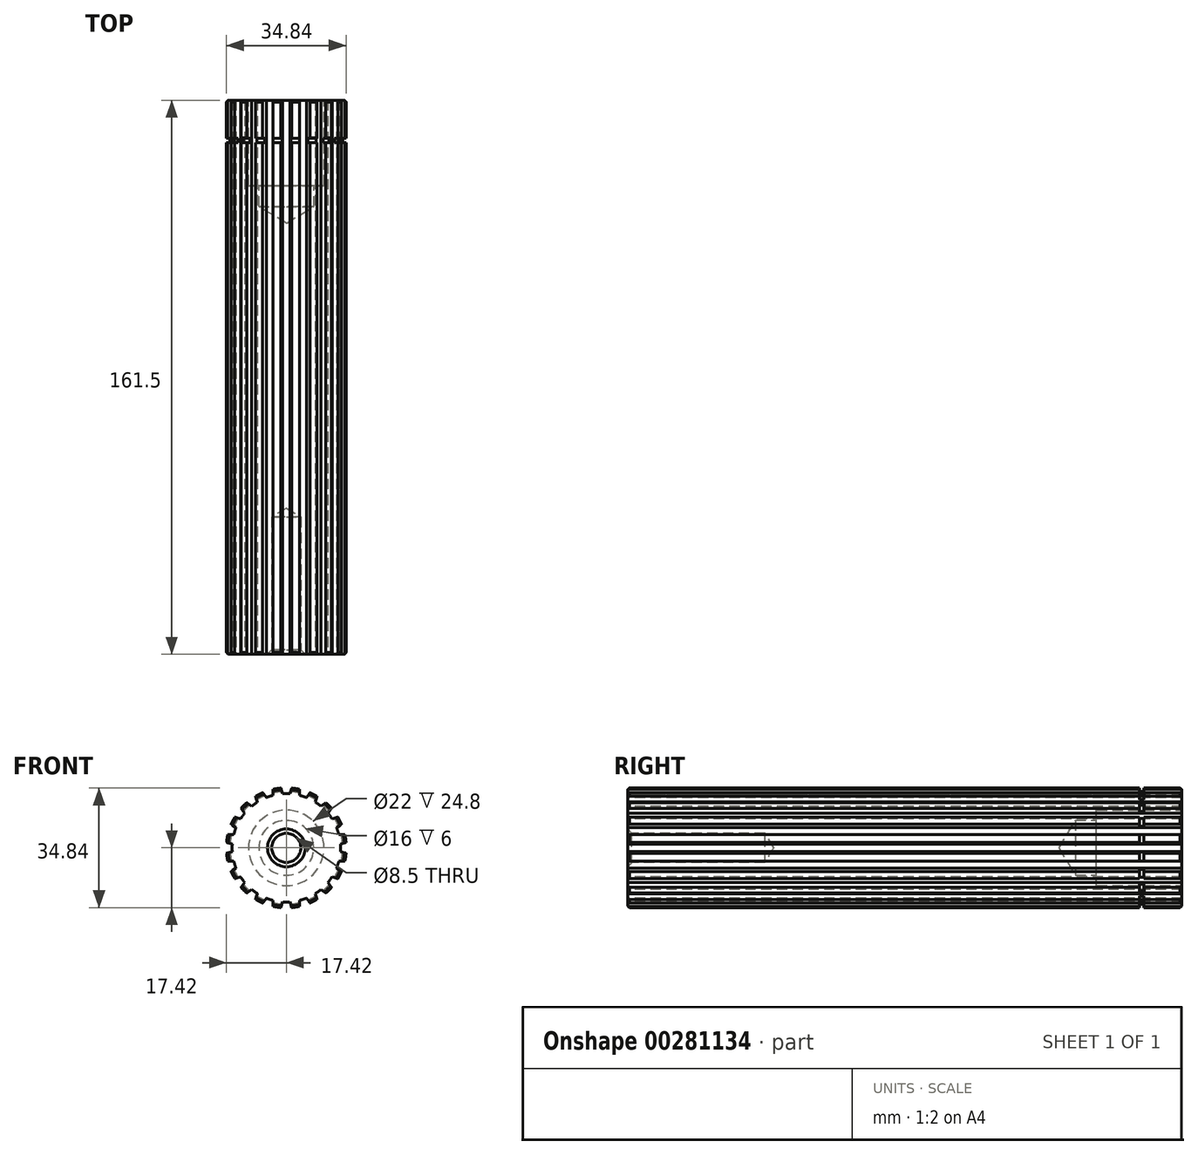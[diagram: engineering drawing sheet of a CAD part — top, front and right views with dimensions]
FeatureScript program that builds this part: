
annotation { "Feature Type Name" : "Feature", "Feature Type Description" : "" }
export const myFeature = defineFeature(function(context is Context, id is Id, definition is map)
    precondition{}
    {
        {
            var Q0;
            Q0=qCreatedBy(makeId("Front.planeOp"),FACE);
            var sketch = newSketch(context, id + "F0", { "sketchPlane" : qUnion([Q0])});
            skArc(sketch, "E0", {"start": v(-5.85, -14.65) * mm, "mid": v(-4.88, -15) * mm, "end": v(-3.88, -15.3) * mm});
            skLineSegment(sketch, "E1", {"start": v(-3.88, -15.3) * mm, "end": v(-3.88, -17.06) * mm});
            skLineSegment(sketch, "E2", {"start": v(-6.89, -16.08) * mm, "end": v(-5.85, -14.65) * mm});
            skArc(sketch, "E3", {"start": v(-3.88, -17.06) * mm, "mid": v(-2.74, -17.28) * mm, "end": v(-1.58, -17.42) * mm});
            skLineSegment(sketch, "E4", {"start": v(-1.58, -17.42) * mm, "end": v(-1.04, -15.75) * mm});
            skArc(sketch, "E5", {"start": v(-1.04, -15.75) * mm, "mid": v(0, -15.78) * mm, "end": v(1.04, -15.75) * mm});
            skLineSegment(sketch, "E6", {"start": v(1.04, -15.75) * mm, "end": v(1.58, -17.42) * mm});
            skArc(sketch, "E7", {"start": v(1.58, -17.42) * mm, "mid": v(2.74, -17.28) * mm, "end": v(3.88, -17.06) * mm});
            skLineSegment(sketch, "E8", {"start": v(3.88, -17.06) * mm, "end": v(3.88, -15.3) * mm});
            skArc(sketch, "E9", {"start": v(3.88, -15.3) * mm, "mid": v(4.88, -15) * mm, "end": v(5.85, -14.65) * mm});
            skLineSegment(sketch, "E10", {"start": v(5.85, -14.65) * mm, "end": v(6.89, -16.08) * mm});
            skArc(sketch, "E11", {"start": v(6.89, -16.08) * mm, "mid": v(7.94, -15.59) * mm, "end": v(8.96, -15.02) * mm});
            skLineSegment(sketch, "E12", {"start": v(8.96, -15.02) * mm, "end": v(8.42, -13.35) * mm});
            skArc(sketch, "E13", {"start": v(8.42, -13.35) * mm, "mid": v(9.28, -12.77) * mm, "end": v(10.1, -12.13) * mm});
            skLineSegment(sketch, "E14", {"start": v(10.1, -12.13) * mm, "end": v(11.52, -13.17) * mm});
            skArc(sketch, "E15", {"start": v(11.52, -13.17) * mm, "mid": v(12.37, -12.37) * mm, "end": v(13.17, -11.52) * mm});
            skLineSegment(sketch, "E16", {"start": v(13.17, -11.52) * mm, "end": v(12.13, -10.1) * mm});
            skArc(sketch, "E17", {"start": v(12.13, -10.1) * mm, "mid": v(12.77, -9.28) * mm, "end": v(13.35, -8.42) * mm});
            skLineSegment(sketch, "E18", {"start": v(13.35, -8.42) * mm, "end": v(15.02, -8.96) * mm});
            skArc(sketch, "E19", {"start": v(15.02, -8.96) * mm, "mid": v(15.59, -7.94) * mm, "end": v(16.08, -6.89) * mm});
            skLineSegment(sketch, "E20", {"start": v(16.08, -6.89) * mm, "end": v(14.65, -5.85) * mm});
            skArc(sketch, "E21", {"start": v(14.65, -5.85) * mm, "mid": v(15, -4.88) * mm, "end": v(15.3, -3.88) * mm});
            skLineSegment(sketch, "E22", {"start": v(15.3, -3.88) * mm, "end": v(17.06, -3.88) * mm});
            skArc(sketch, "E23", {"start": v(17.06, -3.88) * mm, "mid": v(17.28, -2.74) * mm, "end": v(17.42, -1.58) * mm});
            skLineSegment(sketch, "E24", {"start": v(17.42, -1.58) * mm, "end": v(15.75, -1.04) * mm});
            skArc(sketch, "E25", {"start": v(15.75, -1.04) * mm, "mid": v(15.78, 0) * mm, "end": v(15.75, 1.04) * mm});
            skLineSegment(sketch, "E26", {"start": v(15.75, 1.04) * mm, "end": v(17.42, 1.58) * mm});
            skArc(sketch, "E27", {"start": v(17.42, 1.58) * mm, "mid": v(17.28, 2.74) * mm, "end": v(17.06, 3.88) * mm});
            skLineSegment(sketch, "E28", {"start": v(17.06, 3.88) * mm, "end": v(15.3, 3.88) * mm});
            skArc(sketch, "E29", {"start": v(15.3, 3.88) * mm, "mid": v(15, 4.88) * mm, "end": v(14.65, 5.85) * mm});
            skLineSegment(sketch, "E30", {"start": v(14.65, 5.85) * mm, "end": v(16.08, 6.89) * mm});
            skArc(sketch, "E31", {"start": v(16.08, 6.89) * mm, "mid": v(15.59, 7.94) * mm, "end": v(15.02, 8.96) * mm});
            skLineSegment(sketch, "E32", {"start": v(15.02, 8.96) * mm, "end": v(13.35, 8.42) * mm});
            skArc(sketch, "E33", {"start": v(13.35, 8.42) * mm, "mid": v(12.77, 9.28) * mm, "end": v(12.13, 10.1) * mm});
            skLineSegment(sketch, "E34", {"start": v(12.13, 10.1) * mm, "end": v(13.17, 11.52) * mm});
            skArc(sketch, "E35", {"start": v(13.17, 11.52) * mm, "mid": v(12.37, 12.37) * mm, "end": v(11.52, 13.17) * mm});
            skLineSegment(sketch, "E36", {"start": v(11.52, 13.17) * mm, "end": v(10.1, 12.13) * mm});
            skArc(sketch, "E37", {"start": v(10.1, 12.13) * mm, "mid": v(9.28, 12.77) * mm, "end": v(8.42, 13.35) * mm});
            skLineSegment(sketch, "E38", {"start": v(8.42, 13.35) * mm, "end": v(8.96, 15.02) * mm});
            skArc(sketch, "E39", {"start": v(8.96, 15.02) * mm, "mid": v(7.94, 15.59) * mm, "end": v(6.89, 16.08) * mm});
            skLineSegment(sketch, "E40", {"start": v(6.89, 16.08) * mm, "end": v(5.85, 14.65) * mm});
            skArc(sketch, "E41", {"start": v(5.85, 14.65) * mm, "mid": v(4.88, 15) * mm, "end": v(3.88, 15.3) * mm});
            skLineSegment(sketch, "E42", {"start": v(3.88, 15.3) * mm, "end": v(3.88, 17.06) * mm});
            skArc(sketch, "E43", {"start": v(3.88, 17.06) * mm, "mid": v(2.74, 17.28) * mm, "end": v(1.58, 17.42) * mm});
            skLineSegment(sketch, "E44", {"start": v(1.58, 17.42) * mm, "end": v(1.04, 15.75) * mm});
            skArc(sketch, "E45", {"start": v(1.04, 15.75) * mm, "mid": v(0, 15.78) * mm, "end": v(-1.04, 15.75) * mm});
            skLineSegment(sketch, "E46", {"start": v(-1.04, 15.75) * mm, "end": v(-1.58, 17.42) * mm});
            skArc(sketch, "E47", {"start": v(-1.58, 17.42) * mm, "mid": v(-2.74, 17.28) * mm, "end": v(-3.88, 17.06) * mm});
            skLineSegment(sketch, "E48", {"start": v(-3.88, 17.06) * mm, "end": v(-3.88, 15.3) * mm});
            skArc(sketch, "E49", {"start": v(-3.88, 15.3) * mm, "mid": v(-4.88, 15) * mm, "end": v(-5.85, 14.65) * mm});
            skLineSegment(sketch, "E50", {"start": v(-5.85, 14.65) * mm, "end": v(-6.89, 16.08) * mm});
            skArc(sketch, "E51", {"start": v(-6.89, 16.08) * mm, "mid": v(-7.94, 15.59) * mm, "end": v(-8.96, 15.02) * mm});
            skLineSegment(sketch, "E52", {"start": v(-8.96, 15.02) * mm, "end": v(-8.42, 13.35) * mm});
            skArc(sketch, "E53", {"start": v(-8.42, 13.35) * mm, "mid": v(-9.28, 12.77) * mm, "end": v(-10.1, 12.13) * mm});
            skLineSegment(sketch, "E54", {"start": v(-10.1, 12.13) * mm, "end": v(-11.52, 13.17) * mm});
            skArc(sketch, "E55", {"start": v(-11.52, 13.17) * mm, "mid": v(-12.37, 12.37) * mm, "end": v(-13.17, 11.52) * mm});
            skLineSegment(sketch, "E56", {"start": v(-13.17, 11.52) * mm, "end": v(-12.13, 10.1) * mm});
            skArc(sketch, "E57", {"start": v(-12.13, 10.1) * mm, "mid": v(-12.77, 9.28) * mm, "end": v(-13.35, 8.42) * mm});
            skLineSegment(sketch, "E58", {"start": v(-13.35, 8.42) * mm, "end": v(-15.02, 8.96) * mm});
            skArc(sketch, "E59", {"start": v(-15.02, 8.96) * mm, "mid": v(-15.59, 7.94) * mm, "end": v(-16.08, 6.89) * mm});
            skLineSegment(sketch, "E60", {"start": v(-16.08, 6.89) * mm, "end": v(-14.65, 5.85) * mm});
            skArc(sketch, "E61", {"start": v(-14.65, 5.85) * mm, "mid": v(-15, 4.88) * mm, "end": v(-15.3, 3.88) * mm});
            skLineSegment(sketch, "E62", {"start": v(-15.3, 3.88) * mm, "end": v(-17.06, 3.88) * mm});
            skArc(sketch, "E63", {"start": v(-17.06, 3.88) * mm, "mid": v(-17.28, 2.74) * mm, "end": v(-17.42, 1.58) * mm});
            skLineSegment(sketch, "E64", {"start": v(-17.42, 1.58) * mm, "end": v(-15.75, 1.04) * mm});
            skArc(sketch, "E65", {"start": v(-15.75, 1.04) * mm, "mid": v(-15.78, 0) * mm, "end": v(-15.75, -1.04) * mm});
            skLineSegment(sketch, "E66", {"start": v(-15.75, -1.04) * mm, "end": v(-17.42, -1.58) * mm});
            skArc(sketch, "E67", {"start": v(-17.42, -1.58) * mm, "mid": v(-17.28, -2.74) * mm, "end": v(-17.06, -3.88) * mm});
            skLineSegment(sketch, "E68", {"start": v(-17.06, -3.88) * mm, "end": v(-15.3, -3.88) * mm});
            skArc(sketch, "E69", {"start": v(-15.3, -3.88) * mm, "mid": v(-15, -4.88) * mm, "end": v(-14.65, -5.85) * mm});
            skLineSegment(sketch, "E70", {"start": v(-14.65, -5.85) * mm, "end": v(-16.08, -6.89) * mm});
            skArc(sketch, "E71", {"start": v(-16.08, -6.89) * mm, "mid": v(-15.59, -7.94) * mm, "end": v(-15.02, -8.96) * mm});
            skLineSegment(sketch, "E72", {"start": v(-15.02, -8.96) * mm, "end": v(-13.35, -8.42) * mm});
            skArc(sketch, "E73", {"start": v(-13.35, -8.42) * mm, "mid": v(-12.77, -9.28) * mm, "end": v(-12.13, -10.1) * mm});
            skLineSegment(sketch, "E74", {"start": v(-12.13, -10.1) * mm, "end": v(-13.17, -11.52) * mm});
            skArc(sketch, "E75", {"start": v(-13.17, -11.52) * mm, "mid": v(-12.37, -12.37) * mm, "end": v(-11.52, -13.17) * mm});
            skLineSegment(sketch, "E76", {"start": v(-11.52, -13.17) * mm, "end": v(-10.1, -12.13) * mm});
            skArc(sketch, "E77", {"start": v(-10.1, -12.13) * mm, "mid": v(-9.28, -12.77) * mm, "end": v(-8.42, -13.35) * mm});
            skLineSegment(sketch, "E78", {"start": v(-8.42, -13.35) * mm, "end": v(-8.96, -15.02) * mm});
            skArc(sketch, "E79", {"start": v(-8.96, -15.02) * mm, "mid": v(-7.94, -15.59) * mm, "end": v(-6.89, -16.08) * mm});
            skLineSegment(sketch, "E80", {"start": v(0, -20.5) * mm, "end": v(0, 20.5) * mm, "construction": true});
            skLineSegment(sketch, "E81", {"start": v(-20.5, 0) * mm, "end": v(20.5, 0) * mm, "construction": true});
            skSolve(sketch);
        }
        {
            var Q0;
            Q0 = qSketchRegion(id + "F0", true);
            extrude(context, id + "F1", {"entities" : qUnion([Q0]), "oppositeDirection" : true, "depth" : 161.5 * mm});
        }
        {
            var Q0;
            Q0=makeQuery(id+"F1.opExtrude","CAP_FACE",FACE,{"disambiguationData":[OSD([sQuery(id+"F0.wireOp",EDGE,"E0"),sQuery(id+"F0.wireOp",EDGE,"E1"),sQuery(id+"F0.wireOp",EDGE,"E2"),sQuery(id+"F0.wireOp",EDGE,"E3"),sQuery(id+"F0.wireOp",EDGE,"E4"),sQuery(id+"F0.wireOp",EDGE,"E5"),sQuery(id+"F0.wireOp",EDGE,"E6"),sQuery(id+"F0.wireOp",EDGE,"E7"),sQuery(id+"F0.wireOp",EDGE,"E8"),sQuery(id+"F0.wireOp",EDGE,"E9"),sQuery(id+"F0.wireOp",EDGE,"E10"),sQuery(id+"F0.wireOp",EDGE,"E11"),sQuery(id+"F0.wireOp",EDGE,"E12"),sQuery(id+"F0.wireOp",EDGE,"E13"),sQuery(id+"F0.wireOp",EDGE,"E14"),sQuery(id+"F0.wireOp",EDGE,"E15"),sQuery(id+"F0.wireOp",EDGE,"E16"),sQuery(id+"F0.wireOp",EDGE,"E17"),sQuery(id+"F0.wireOp",EDGE,"E18"),sQuery(id+"F0.wireOp",EDGE,"E19"),sQuery(id+"F0.wireOp",EDGE,"E20"),sQuery(id+"F0.wireOp",EDGE,"E21"),sQuery(id+"F0.wireOp",EDGE,"E22"),sQuery(id+"F0.wireOp",EDGE,"E23"),sQuery(id+"F0.wireOp",EDGE,"E24"),sQuery(id+"F0.wireOp",EDGE,"E25"),sQuery(id+"F0.wireOp",EDGE,"E26"),sQuery(id+"F0.wireOp",EDGE,"E27"),sQuery(id+"F0.wireOp",EDGE,"E28"),sQuery(id+"F0.wireOp",EDGE,"E29"),sQuery(id+"F0.wireOp",EDGE,"E30"),sQuery(id+"F0.wireOp",EDGE,"E31"),sQuery(id+"F0.wireOp",EDGE,"E32"),sQuery(id+"F0.wireOp",EDGE,"E33"),sQuery(id+"F0.wireOp",EDGE,"E34"),sQuery(id+"F0.wireOp",EDGE,"E35"),sQuery(id+"F0.wireOp",EDGE,"E36"),sQuery(id+"F0.wireOp",EDGE,"E37"),sQuery(id+"F0.wireOp",EDGE,"E38"),sQuery(id+"F0.wireOp",EDGE,"E39"),sQuery(id+"F0.wireOp",EDGE,"E40"),sQuery(id+"F0.wireOp",EDGE,"E41"),sQuery(id+"F0.wireOp",EDGE,"E42"),sQuery(id+"F0.wireOp",EDGE,"E43"),sQuery(id+"F0.wireOp",EDGE,"E44"),sQuery(id+"F0.wireOp",EDGE,"E45"),sQuery(id+"F0.wireOp",EDGE,"E46"),sQuery(id+"F0.wireOp",EDGE,"E47"),sQuery(id+"F0.wireOp",EDGE,"E48"),sQuery(id+"F0.wireOp",EDGE,"E49"),sQuery(id+"F0.wireOp",EDGE,"E50"),sQuery(id+"F0.wireOp",EDGE,"E51"),sQuery(id+"F0.wireOp",EDGE,"E52"),sQuery(id+"F0.wireOp",EDGE,"E53"),sQuery(id+"F0.wireOp",EDGE,"E54"),sQuery(id+"F0.wireOp",EDGE,"E55"),sQuery(id+"F0.wireOp",EDGE,"E56"),sQuery(id+"F0.wireOp",EDGE,"E57"),sQuery(id+"F0.wireOp",EDGE,"E58"),sQuery(id+"F0.wireOp",EDGE,"E59"),sQuery(id+"F0.wireOp",EDGE,"E60"),sQuery(id+"F0.wireOp",EDGE,"E61"),sQuery(id+"F0.wireOp",EDGE,"E62"),sQuery(id+"F0.wireOp",EDGE,"E63"),sQuery(id+"F0.wireOp",EDGE,"E64"),sQuery(id+"F0.wireOp",EDGE,"E65"),sQuery(id+"F0.wireOp",EDGE,"E66"),sQuery(id+"F0.wireOp",EDGE,"E67"),sQuery(id+"F0.wireOp",EDGE,"E68"),sQuery(id+"F0.wireOp",EDGE,"E69"),sQuery(id+"F0.wireOp",EDGE,"E70"),sQuery(id+"F0.wireOp",EDGE,"E71"),sQuery(id+"F0.wireOp",EDGE,"E72"),sQuery(id+"F0.wireOp",EDGE,"E73"),sQuery(id+"F0.wireOp",EDGE,"E74"),sQuery(id+"F0.wireOp",EDGE,"E75"),sQuery(id+"F0.wireOp",EDGE,"E76"),sQuery(id+"F0.wireOp",EDGE,"E77"),sQuery(id+"F0.wireOp",EDGE,"E78"),sQuery(id+"F0.wireOp",EDGE,"E79")])],"isStart":false});
            var sketch = newSketch(context, id + "F2", { "sketchPlane" : qUnion([Q0])});
            skPoint(sketch, "E82", {"position": v(0, 0) * mm});
            skCircle(sketch, "E83", {"center": v(0, 0) * mm, "radius": 11 * mm});
            skSolve(sketch);
        }
        {
            var Q0;
            Q0=sQuery(id+"F2.wireOp",VERTEX,"E82");
            var Q1;
            Q1=makeQuery(id+"F1.opExtrude","SWEPT_BODY",BODY,{"disambiguationData":[OSD([sQuery(id+"F0.wireOp",EDGE,"E0"),sQuery(id+"F0.wireOp",EDGE,"E1"),sQuery(id+"F0.wireOp",EDGE,"E2"),sQuery(id+"F0.wireOp",EDGE,"E3"),sQuery(id+"F0.wireOp",EDGE,"E4"),sQuery(id+"F0.wireOp",EDGE,"E5"),sQuery(id+"F0.wireOp",EDGE,"E6"),sQuery(id+"F0.wireOp",EDGE,"E7"),sQuery(id+"F0.wireOp",EDGE,"E8"),sQuery(id+"F0.wireOp",EDGE,"E9"),sQuery(id+"F0.wireOp",EDGE,"E10"),sQuery(id+"F0.wireOp",EDGE,"E11"),sQuery(id+"F0.wireOp",EDGE,"E12"),sQuery(id+"F0.wireOp",EDGE,"E13"),sQuery(id+"F0.wireOp",EDGE,"E14"),sQuery(id+"F0.wireOp",EDGE,"E15"),sQuery(id+"F0.wireOp",EDGE,"E16"),sQuery(id+"F0.wireOp",EDGE,"E17"),sQuery(id+"F0.wireOp",EDGE,"E18"),sQuery(id+"F0.wireOp",EDGE,"E19"),sQuery(id+"F0.wireOp",EDGE,"E20"),sQuery(id+"F0.wireOp",EDGE,"E21"),sQuery(id+"F0.wireOp",EDGE,"E22"),sQuery(id+"F0.wireOp",EDGE,"E23"),sQuery(id+"F0.wireOp",EDGE,"E24"),sQuery(id+"F0.wireOp",EDGE,"E25"),sQuery(id+"F0.wireOp",EDGE,"E26"),sQuery(id+"F0.wireOp",EDGE,"E27"),sQuery(id+"F0.wireOp",EDGE,"E28"),sQuery(id+"F0.wireOp",EDGE,"E29"),sQuery(id+"F0.wireOp",EDGE,"E30"),sQuery(id+"F0.wireOp",EDGE,"E31"),sQuery(id+"F0.wireOp",EDGE,"E32"),sQuery(id+"F0.wireOp",EDGE,"E33"),sQuery(id+"F0.wireOp",EDGE,"E34"),sQuery(id+"F0.wireOp",EDGE,"E35"),sQuery(id+"F0.wireOp",EDGE,"E36"),sQuery(id+"F0.wireOp",EDGE,"E37"),sQuery(id+"F0.wireOp",EDGE,"E38"),sQuery(id+"F0.wireOp",EDGE,"E39"),sQuery(id+"F0.wireOp",EDGE,"E40"),sQuery(id+"F0.wireOp",EDGE,"E41"),sQuery(id+"F0.wireOp",EDGE,"E42"),sQuery(id+"F0.wireOp",EDGE,"E43"),sQuery(id+"F0.wireOp",EDGE,"E44"),sQuery(id+"F0.wireOp",EDGE,"E45"),sQuery(id+"F0.wireOp",EDGE,"E46"),sQuery(id+"F0.wireOp",EDGE,"E47"),sQuery(id+"F0.wireOp",EDGE,"E48"),sQuery(id+"F0.wireOp",EDGE,"E49"),sQuery(id+"F0.wireOp",EDGE,"E50"),sQuery(id+"F0.wireOp",EDGE,"E51"),sQuery(id+"F0.wireOp",EDGE,"E52"),sQuery(id+"F0.wireOp",EDGE,"E53"),sQuery(id+"F0.wireOp",EDGE,"E54"),sQuery(id+"F0.wireOp",EDGE,"E55"),sQuery(id+"F0.wireOp",EDGE,"E56"),sQuery(id+"F0.wireOp",EDGE,"E57"),sQuery(id+"F0.wireOp",EDGE,"E58"),sQuery(id+"F0.wireOp",EDGE,"E59"),sQuery(id+"F0.wireOp",EDGE,"E60"),sQuery(id+"F0.wireOp",EDGE,"E61"),sQuery(id+"F0.wireOp",EDGE,"E62"),sQuery(id+"F0.wireOp",EDGE,"E63"),sQuery(id+"F0.wireOp",EDGE,"E64"),sQuery(id+"F0.wireOp",EDGE,"E65"),sQuery(id+"F0.wireOp",EDGE,"E66"),sQuery(id+"F0.wireOp",EDGE,"E67"),sQuery(id+"F0.wireOp",EDGE,"E68"),sQuery(id+"F0.wireOp",EDGE,"E69"),sQuery(id+"F0.wireOp",EDGE,"E70"),sQuery(id+"F0.wireOp",EDGE,"E71"),sQuery(id+"F0.wireOp",EDGE,"E72"),sQuery(id+"F0.wireOp",EDGE,"E73"),sQuery(id+"F0.wireOp",EDGE,"E74"),sQuery(id+"F0.wireOp",EDGE,"E75"),sQuery(id+"F0.wireOp",EDGE,"E76"),sQuery(id+"F0.wireOp",EDGE,"E77"),sQuery(id+"F0.wireOp",EDGE,"E78"),sQuery(id+"F0.wireOp",EDGE,"E79")])]});
            hole(context, id + "F3", {"style" : HoleStyle.C_SINK, "endStyle" : HoleEndStyle.BLIND, "holeDiameter" : 16 * mm, "cSinkDiameter" : 17 * mm, "cSinkAngle" : 90 * degree, "holeDepth" : 31 * mm, "tappedDepth" : 12 * mm, "tapClearance" : 3, "locations" : qUnion([Q0]), "scope" : qUnion([Q1])});
        }
        {
            var Q0;
            Q0=makeQuery(id+"F2.imprint","IMPRINT",FACE,{"disambiguationData":[TD([[makeQuery(id+"F2.imprint","IMPRINT",EDGE,{"derivedFrom":sQuery(id+"F2.wireOp",EDGE,"E83")}),1.0]])]});
            extrude(context, id + "F4", {"entities" : qUnion([Q0]), "operationType" : NewBodyOperationType.REMOVE, "oppositeDirection" : true, "depth" : 25 * mm});
        }
        {
            var Q0;
            Q0=makeQuery(id+"F2.imprint","IMPRINT",FACE,{"disambiguationData":[TD([[makeQuery(id+"F2.imprint","IMPRINT",EDGE,{"derivedFrom":sQuery(id+"F2.wireOp",EDGE,"E83")}),-1.0]])]});
            cPlane(context, id + "F5", {"entities" : qUnion([Q0]), "cplaneType" : CPlaneType.OFFSET, "offset" : 11.04 * mm, "oppositeDirection" : true, "width" : 150 * mm, "height" : 150 * mm});
        }
        {
            var Q0;
            Q0=qCreatedBy(id+"F5.planeOp",FACE);
            var sketch = newSketch(context, id + "F6", { "sketchPlane" : qUnion([Q0])});
            skPoint(sketch, "E84.0", {"position": v(0, 0) * mm});
            skCircle(sketch, "E85", {"center": v(0, 0) * mm, "radius": 16.45 * mm});
            skCircle(sketch, "E86", {"center": v(0, 0) * mm, "radius": 17.5 * mm});
            skSolve(sketch);
        }
        {
            var Q0;
            Q0=makeQuery(id+"F6.imprint","IMPRINT",FACE,{"disambiguationData":[TD([[makeQuery(id+"F6.imprint","IMPRINT",EDGE,{"derivedFrom":sQuery(id+"F6.wireOp",EDGE,"E85")}),-1.0]])]});
            extrude(context, id + "F7", {"entities" : qUnion([Q0]), "operationType" : NewBodyOperationType.REMOVE, "oppositeDirection" : true, "depth" : 1.3 * mm});
        }
        {
            var Q0;
            Q0=makeQuery(id+"F4.boolean.opBoolean","COPY",EDGE,{"derivedFrom":makeQuery(id+"F4.opExtrude","CAP_EDGE",EDGE,{"disambiguationData":[OSD([sQuery(id+"F2.wireOp",EDGE,"E83")])],"isStart":true})});
            var Q1;
            Q1=makeQuery(id+"F1.opExtrude","CAP_EDGE",EDGE,{"disambiguationData":[OSD([sQuery(id+"F0.wireOp",EDGE,"E39")])],"isStart":false});
            var Q2;
            Q2=makeQuery(id+"F1.opExtrude","CAP_EDGE",EDGE,{"disambiguationData":[OSD([sQuery(id+"F0.wireOp",EDGE,"E43")])],"isStart":false});
            var Q3;
            Q3=makeQuery(id+"F1.opExtrude","CAP_EDGE",EDGE,{"disambiguationData":[OSD([sQuery(id+"F0.wireOp",EDGE,"E47")])],"isStart":false});
            var Q4;
            Q4=makeQuery(id+"F1.opExtrude","CAP_EDGE",EDGE,{"disambiguationData":[OSD([sQuery(id+"F0.wireOp",EDGE,"E35")])],"isStart":false});
            var Q5;
            Q5=makeQuery(id+"F1.opExtrude","CAP_EDGE",EDGE,{"disambiguationData":[OSD([sQuery(id+"F0.wireOp",EDGE,"E31")])],"isStart":false});
            var Q6;
            Q6=makeQuery(id+"F1.opExtrude","CAP_EDGE",EDGE,{"disambiguationData":[OSD([sQuery(id+"F0.wireOp",EDGE,"E27")])],"isStart":false});
            var Q7;
            Q7=makeQuery(id+"F1.opExtrude","CAP_EDGE",EDGE,{"disambiguationData":[OSD([sQuery(id+"F0.wireOp",EDGE,"E51")])],"isStart":false});
            var Q8;
            Q8=makeQuery(id+"F1.opExtrude","CAP_EDGE",EDGE,{"disambiguationData":[OSD([sQuery(id+"F0.wireOp",EDGE,"E55")])],"isStart":false});
            var Q9;
            Q9=makeQuery(id+"F1.opExtrude","CAP_EDGE",EDGE,{"disambiguationData":[OSD([sQuery(id+"F0.wireOp",EDGE,"E59")])],"isStart":false});
            var Q10;
            Q10=makeQuery(id+"F1.opExtrude","CAP_EDGE",EDGE,{"disambiguationData":[OSD([sQuery(id+"F0.wireOp",EDGE,"E63")])],"isStart":false});
            var Q11;
            Q11=makeQuery(id+"F1.opExtrude","CAP_EDGE",EDGE,{"disambiguationData":[OSD([sQuery(id+"F0.wireOp",EDGE,"E67")])],"isStart":false});
            var Q12;
            Q12=makeQuery(id+"F1.opExtrude","CAP_EDGE",EDGE,{"disambiguationData":[OSD([sQuery(id+"F0.wireOp",EDGE,"E71")])],"isStart":false});
            var Q13;
            Q13=makeQuery(id+"F1.opExtrude","CAP_EDGE",EDGE,{"disambiguationData":[OSD([sQuery(id+"F0.wireOp",EDGE,"E75")])],"isStart":false});
            var Q14;
            Q14=makeQuery(id+"F1.opExtrude","CAP_EDGE",EDGE,{"disambiguationData":[OSD([sQuery(id+"F0.wireOp",EDGE,"E79")])],"isStart":false});
            var Q15;
            Q15=makeQuery(id+"F1.opExtrude","CAP_EDGE",EDGE,{"disambiguationData":[OSD([sQuery(id+"F0.wireOp",EDGE,"E3")])],"isStart":false});
            var Q16;
            Q16=makeQuery(id+"F1.opExtrude","CAP_EDGE",EDGE,{"disambiguationData":[OSD([sQuery(id+"F0.wireOp",EDGE,"E7")])],"isStart":false});
            var Q17;
            Q17=makeQuery(id+"F1.opExtrude","CAP_EDGE",EDGE,{"disambiguationData":[OSD([sQuery(id+"F0.wireOp",EDGE,"E11")])],"isStart":false});
            var Q18;
            Q18=makeQuery(id+"F1.opExtrude","CAP_EDGE",EDGE,{"disambiguationData":[OSD([sQuery(id+"F0.wireOp",EDGE,"E15")])],"isStart":false});
            var Q19;
            Q19=makeQuery(id+"F1.opExtrude","CAP_EDGE",EDGE,{"disambiguationData":[OSD([sQuery(id+"F0.wireOp",EDGE,"E19")])],"isStart":false});
            var Q20;
            Q20=makeQuery(id+"F1.opExtrude","CAP_EDGE",EDGE,{"disambiguationData":[OSD([sQuery(id+"F0.wireOp",EDGE,"E23")])],"isStart":false});
            var Q21;
            Q21=makeQuery(id+"F1.opExtrude","CAP_EDGE",EDGE,{"disambiguationData":[OSD([sQuery(id+"F0.wireOp",EDGE,"E55")])],"isStart":true});
            var Q22;
            Q22=makeQuery(id+"F1.opExtrude","CAP_EDGE",EDGE,{"disambiguationData":[OSD([sQuery(id+"F0.wireOp",EDGE,"E51")])],"isStart":true});
            var Q23;
            Q23=makeQuery(id+"F1.opExtrude","CAP_EDGE",EDGE,{"disambiguationData":[OSD([sQuery(id+"F0.wireOp",EDGE,"E47")])],"isStart":true});
            var Q24;
            Q24=makeQuery(id+"F1.opExtrude","CAP_EDGE",EDGE,{"disambiguationData":[OSD([sQuery(id+"F0.wireOp",EDGE,"E59")])],"isStart":true});
            var Q25;
            Q25=makeQuery(id+"F1.opExtrude","CAP_EDGE",EDGE,{"disambiguationData":[OSD([sQuery(id+"F0.wireOp",EDGE,"E43")])],"isStart":true});
            var Q26;
            Q26=makeQuery(id+"F1.opExtrude","CAP_EDGE",EDGE,{"disambiguationData":[OSD([sQuery(id+"F0.wireOp",EDGE,"E39")])],"isStart":true});
            var Q27;
            Q27=makeQuery(id+"F1.opExtrude","CAP_EDGE",EDGE,{"disambiguationData":[OSD([sQuery(id+"F0.wireOp",EDGE,"E35")])],"isStart":true});
            var Q28;
            Q28=makeQuery(id+"F1.opExtrude","CAP_EDGE",EDGE,{"disambiguationData":[OSD([sQuery(id+"F0.wireOp",EDGE,"E31")])],"isStart":true});
            var Q29;
            Q29=makeQuery(id+"F1.opExtrude","CAP_EDGE",EDGE,{"disambiguationData":[OSD([sQuery(id+"F0.wireOp",EDGE,"E27")])],"isStart":true});
            var Q30;
            Q30=makeQuery(id+"F1.opExtrude","CAP_EDGE",EDGE,{"disambiguationData":[OSD([sQuery(id+"F0.wireOp",EDGE,"E23")])],"isStart":true});
            var Q31;
            Q31=makeQuery(id+"F1.opExtrude","CAP_EDGE",EDGE,{"disambiguationData":[OSD([sQuery(id+"F0.wireOp",EDGE,"E19")])],"isStart":true});
            var Q32;
            Q32=makeQuery(id+"F1.opExtrude","CAP_EDGE",EDGE,{"disambiguationData":[OSD([sQuery(id+"F0.wireOp",EDGE,"E15")])],"isStart":true});
            var Q33;
            Q33=makeQuery(id+"F1.opExtrude","CAP_EDGE",EDGE,{"disambiguationData":[OSD([sQuery(id+"F0.wireOp",EDGE,"E11")])],"isStart":true});
            var Q34;
            Q34=makeQuery(id+"F1.opExtrude","CAP_EDGE",EDGE,{"disambiguationData":[OSD([sQuery(id+"F0.wireOp",EDGE,"E7")])],"isStart":true});
            var Q35;
            Q35=makeQuery(id+"F1.opExtrude","CAP_EDGE",EDGE,{"disambiguationData":[OSD([sQuery(id+"F0.wireOp",EDGE,"E3")])],"isStart":true});
            var Q36;
            Q36=makeQuery(id+"F1.opExtrude","CAP_EDGE",EDGE,{"disambiguationData":[OSD([sQuery(id+"F0.wireOp",EDGE,"E79")])],"isStart":true});
            var Q37;
            Q37=makeQuery(id+"F1.opExtrude","CAP_EDGE",EDGE,{"disambiguationData":[OSD([sQuery(id+"F0.wireOp",EDGE,"E75")])],"isStart":true});
            var Q38;
            Q38=makeQuery(id+"F1.opExtrude","CAP_EDGE",EDGE,{"disambiguationData":[OSD([sQuery(id+"F0.wireOp",EDGE,"E71")])],"isStart":true});
            var Q39;
            Q39=makeQuery(id+"F1.opExtrude","CAP_EDGE",EDGE,{"disambiguationData":[OSD([sQuery(id+"F0.wireOp",EDGE,"E67")])],"isStart":true});
            var Q40;
            Q40=makeQuery(id+"F1.opExtrude","CAP_EDGE",EDGE,{"disambiguationData":[OSD([sQuery(id+"F0.wireOp",EDGE,"E63")])],"isStart":true});
            var Q41;
            Q41=makeQuery(id+"F4.boolean.opBoolean","INTERSECT",EDGE,{"derivedFrom":[makeQuery(id+"F3.hole-0.boolean.opBoolean","COPY",FACE,{"derivedFrom":makeQuery(id+"F3.hole-0.opRevolve","SWEPT_FACE",FACE,{"disambiguationData":[OSD([sQuery(id+"F3.hole-0.sketch.wireOp",EDGE,"core_line_2")])]})}),makeQuery(id+"F4.opExtrude","CAP_FACE",FACE,{"disambiguationData":[OSD([sQuery(id+"F2.wireOp",EDGE,"E83")])],"isStart":false})]});
            chamfer(context, id + "F8", {"entities" : qUnion([Q0, Q1, Q2, Q3, Q4, Q5, Q6, Q7, Q8, Q9, Q10, Q11, Q12, Q13, Q14, Q15, Q16, Q17, Q18, Q19, Q20, Q21, Q22, Q23, Q24, Q25, Q26, Q27, Q28, Q29, Q30, Q31, Q32, Q33, Q34, Q35, Q36, Q37, Q38, Q39, Q40, Q41]), "width" : .5 * mm, "tangentPropagation" : true});
        }
        {
            var Q0;
            Q0=makeQuery(id+"F4.boolean.opBoolean","COPY",EDGE,{"derivedFrom":makeQuery(id+"F4.opExtrude","CAP_EDGE",EDGE,{"disambiguationData":[OSD([sQuery(id+"F2.wireOp",EDGE,"E83")])],"isStart":false})});
            fillet(context, id + "F9", {"entities" : qUnion([Q0]), "radius" : .2 * mm, "tangentPropagation" : true, "allowEdgeOverflow" : false});
        }
        {
            var Q0;
            {var subQ0=sQuery(id+"F6.wireOp",EDGE,"E86");Q0=makeQuery(id+"F7.boolean.opBoolean","COPY",EDGE,{"disambiguationData":[topologyDisambiguationEdgeConnected([makeQuery(id+"F1.opExtrude","SWEPT_FACE",FACE,{"disambiguationData":[OSD([sQuery(id+"F0.wireOp",EDGE,"E47")])]})])],"derivedFrom":makeQuery(id+"F7.opExtrude","CAP_EDGE",EDGE,{"disambiguationData":[OSD([subQ0])],"isStart":false})});}
            var Q1;
            {var subQ0=sQuery(id+"F6.wireOp",EDGE,"E86");Q1=makeQuery(id+"F7.boolean.opBoolean","COPY",EDGE,{"disambiguationData":[topologyDisambiguationEdgeConnected([makeQuery(id+"F1.opExtrude","SWEPT_FACE",FACE,{"disambiguationData":[OSD([sQuery(id+"F0.wireOp",EDGE,"E47")])]})])],"derivedFrom":makeQuery(id+"F7.opExtrude","CAP_EDGE",EDGE,{"disambiguationData":[OSD([subQ0])],"isStart":true})});}
            var Q2;
            {var subQ0=sQuery(id+"F6.wireOp",EDGE,"E86");Q2=makeQuery(id+"F7.boolean.opBoolean","COPY",EDGE,{"disambiguationData":[topologyDisambiguationEdgeConnected([makeQuery(id+"F1.opExtrude","SWEPT_FACE",FACE,{"disambiguationData":[OSD([sQuery(id+"F0.wireOp",EDGE,"E43")])]})])],"derivedFrom":makeQuery(id+"F7.opExtrude","CAP_EDGE",EDGE,{"disambiguationData":[OSD([subQ0])],"isStart":true})});}
            var Q3;
            {var subQ0=sQuery(id+"F6.wireOp",EDGE,"E86");Q3=makeQuery(id+"F7.boolean.opBoolean","COPY",EDGE,{"disambiguationData":[topologyDisambiguationEdgeConnected([makeQuery(id+"F1.opExtrude","SWEPT_FACE",FACE,{"disambiguationData":[OSD([sQuery(id+"F0.wireOp",EDGE,"E43")])]})])],"derivedFrom":makeQuery(id+"F7.opExtrude","CAP_EDGE",EDGE,{"disambiguationData":[OSD([subQ0])],"isStart":false})});}
            var Q4;
            {var subQ0=sQuery(id+"F6.wireOp",EDGE,"E86");Q4=makeQuery(id+"F7.boolean.opBoolean","COPY",EDGE,{"disambiguationData":[topologyDisambiguationEdgeConnected([makeQuery(id+"F1.opExtrude","SWEPT_FACE",FACE,{"disambiguationData":[OSD([sQuery(id+"F0.wireOp",EDGE,"E39")])]})])],"derivedFrom":makeQuery(id+"F7.opExtrude","CAP_EDGE",EDGE,{"disambiguationData":[OSD([subQ0])],"isStart":false})});}
            var Q5;
            {var subQ0=sQuery(id+"F6.wireOp",EDGE,"E86");Q5=makeQuery(id+"F7.boolean.opBoolean","COPY",EDGE,{"disambiguationData":[topologyDisambiguationEdgeConnected([makeQuery(id+"F1.opExtrude","SWEPT_FACE",FACE,{"disambiguationData":[OSD([sQuery(id+"F0.wireOp",EDGE,"E39")])]})])],"derivedFrom":makeQuery(id+"F7.opExtrude","CAP_EDGE",EDGE,{"disambiguationData":[OSD([subQ0])],"isStart":true})});}
            var Q6;
            {var subQ0=sQuery(id+"F6.wireOp",EDGE,"E86");Q6=makeQuery(id+"F7.boolean.opBoolean","COPY",EDGE,{"disambiguationData":[topologyDisambiguationEdgeConnected([makeQuery(id+"F1.opExtrude","SWEPT_FACE",FACE,{"disambiguationData":[OSD([sQuery(id+"F0.wireOp",EDGE,"E31")])]})])],"derivedFrom":makeQuery(id+"F7.opExtrude","CAP_EDGE",EDGE,{"disambiguationData":[OSD([subQ0])],"isStart":false})});}
            var Q7;
            {var subQ0=sQuery(id+"F6.wireOp",EDGE,"E86");Q7=makeQuery(id+"F7.boolean.opBoolean","COPY",EDGE,{"disambiguationData":[topologyDisambiguationEdgeConnected([makeQuery(id+"F1.opExtrude","SWEPT_FACE",FACE,{"disambiguationData":[OSD([sQuery(id+"F0.wireOp",EDGE,"E31")])]})])],"derivedFrom":makeQuery(id+"F7.opExtrude","CAP_EDGE",EDGE,{"disambiguationData":[OSD([subQ0])],"isStart":true})});}
            var Q8;
            {var subQ0=sQuery(id+"F6.wireOp",EDGE,"E86");Q8=makeQuery(id+"F7.boolean.opBoolean","COPY",EDGE,{"disambiguationData":[topologyDisambiguationEdgeConnected([makeQuery(id+"F1.opExtrude","SWEPT_FACE",FACE,{"disambiguationData":[OSD([sQuery(id+"F0.wireOp",EDGE,"E35")])]})])],"derivedFrom":makeQuery(id+"F7.opExtrude","CAP_EDGE",EDGE,{"disambiguationData":[OSD([subQ0])],"isStart":false})});}
            var Q9;
            {var subQ0=sQuery(id+"F6.wireOp",EDGE,"E86");Q9=makeQuery(id+"F7.boolean.opBoolean","COPY",EDGE,{"disambiguationData":[topologyDisambiguationEdgeConnected([makeQuery(id+"F1.opExtrude","SWEPT_FACE",FACE,{"disambiguationData":[OSD([sQuery(id+"F0.wireOp",EDGE,"E35")])]})])],"derivedFrom":makeQuery(id+"F7.opExtrude","CAP_EDGE",EDGE,{"disambiguationData":[OSD([subQ0])],"isStart":true})});}
            var Q10;
            {var subQ0=sQuery(id+"F6.wireOp",EDGE,"E86");Q10=makeQuery(id+"F7.boolean.opBoolean","COPY",EDGE,{"disambiguationData":[topologyDisambiguationEdgeConnected([makeQuery(id+"F1.opExtrude","SWEPT_FACE",FACE,{"disambiguationData":[OSD([sQuery(id+"F0.wireOp",EDGE,"E27")])]})])],"derivedFrom":makeQuery(id+"F7.opExtrude","CAP_EDGE",EDGE,{"disambiguationData":[OSD([subQ0])],"isStart":false})});}
            var Q11;
            {var subQ0=sQuery(id+"F6.wireOp",EDGE,"E86");Q11=makeQuery(id+"F7.boolean.opBoolean","COPY",EDGE,{"disambiguationData":[topologyDisambiguationEdgeConnected([makeQuery(id+"F1.opExtrude","SWEPT_FACE",FACE,{"disambiguationData":[OSD([sQuery(id+"F0.wireOp",EDGE,"E27")])]})])],"derivedFrom":makeQuery(id+"F7.opExtrude","CAP_EDGE",EDGE,{"disambiguationData":[OSD([subQ0])],"isStart":true})});}
            var Q12;
            {var subQ0=sQuery(id+"F6.wireOp",EDGE,"E86");Q12=makeQuery(id+"F7.boolean.opBoolean","COPY",EDGE,{"disambiguationData":[topologyDisambiguationEdgeConnected([makeQuery(id+"F1.opExtrude","SWEPT_FACE",FACE,{"disambiguationData":[OSD([sQuery(id+"F0.wireOp",EDGE,"E23")])]})])],"derivedFrom":makeQuery(id+"F7.opExtrude","CAP_EDGE",EDGE,{"disambiguationData":[OSD([subQ0])],"isStart":false})});}
            var Q13;
            {var subQ0=sQuery(id+"F6.wireOp",EDGE,"E86");Q13=makeQuery(id+"F7.boolean.opBoolean","COPY",EDGE,{"disambiguationData":[topologyDisambiguationEdgeConnected([makeQuery(id+"F1.opExtrude","SWEPT_FACE",FACE,{"disambiguationData":[OSD([sQuery(id+"F0.wireOp",EDGE,"E23")])]})])],"derivedFrom":makeQuery(id+"F7.opExtrude","CAP_EDGE",EDGE,{"disambiguationData":[OSD([subQ0])],"isStart":true})});}
            var Q14;
            {var subQ0=sQuery(id+"F6.wireOp",EDGE,"E86");Q14=makeQuery(id+"F7.boolean.opBoolean","COPY",EDGE,{"disambiguationData":[topologyDisambiguationEdgeConnected([makeQuery(id+"F1.opExtrude","SWEPT_FACE",FACE,{"disambiguationData":[OSD([sQuery(id+"F0.wireOp",EDGE,"E19")])]})])],"derivedFrom":makeQuery(id+"F7.opExtrude","CAP_EDGE",EDGE,{"disambiguationData":[OSD([subQ0])],"isStart":false})});}
            var Q15;
            {var subQ0=sQuery(id+"F6.wireOp",EDGE,"E86");Q15=makeQuery(id+"F7.boolean.opBoolean","COPY",EDGE,{"disambiguationData":[topologyDisambiguationEdgeConnected([makeQuery(id+"F1.opExtrude","SWEPT_FACE",FACE,{"disambiguationData":[OSD([sQuery(id+"F0.wireOp",EDGE,"E19")])]})])],"derivedFrom":makeQuery(id+"F7.opExtrude","CAP_EDGE",EDGE,{"disambiguationData":[OSD([subQ0])],"isStart":true})});}
            var Q16;
            {var subQ0=sQuery(id+"F6.wireOp",EDGE,"E86");Q16=makeQuery(id+"F7.boolean.opBoolean","COPY",EDGE,{"disambiguationData":[topologyDisambiguationEdgeConnected([makeQuery(id+"F1.opExtrude","SWEPT_FACE",FACE,{"disambiguationData":[OSD([sQuery(id+"F0.wireOp",EDGE,"E15")])]})])],"derivedFrom":makeQuery(id+"F7.opExtrude","CAP_EDGE",EDGE,{"disambiguationData":[OSD([subQ0])],"isStart":false})});}
            var Q17;
            {var subQ0=sQuery(id+"F6.wireOp",EDGE,"E86");Q17=makeQuery(id+"F7.boolean.opBoolean","COPY",EDGE,{"disambiguationData":[topologyDisambiguationEdgeConnected([makeQuery(id+"F1.opExtrude","SWEPT_FACE",FACE,{"disambiguationData":[OSD([sQuery(id+"F0.wireOp",EDGE,"E15")])]})])],"derivedFrom":makeQuery(id+"F7.opExtrude","CAP_EDGE",EDGE,{"disambiguationData":[OSD([subQ0])],"isStart":true})});}
            var Q18;
            {var subQ0=sQuery(id+"F6.wireOp",EDGE,"E86");Q18=makeQuery(id+"F7.boolean.opBoolean","COPY",EDGE,{"disambiguationData":[topologyDisambiguationEdgeConnected([makeQuery(id+"F1.opExtrude","SWEPT_FACE",FACE,{"disambiguationData":[OSD([sQuery(id+"F0.wireOp",EDGE,"E11")])]})])],"derivedFrom":makeQuery(id+"F7.opExtrude","CAP_EDGE",EDGE,{"disambiguationData":[OSD([subQ0])],"isStart":false})});}
            var Q19;
            {var subQ0=sQuery(id+"F6.wireOp",EDGE,"E86");Q19=makeQuery(id+"F7.boolean.opBoolean","COPY",EDGE,{"disambiguationData":[topologyDisambiguationEdgeConnected([makeQuery(id+"F1.opExtrude","SWEPT_FACE",FACE,{"disambiguationData":[OSD([sQuery(id+"F0.wireOp",EDGE,"E11")])]})])],"derivedFrom":makeQuery(id+"F7.opExtrude","CAP_EDGE",EDGE,{"disambiguationData":[OSD([subQ0])],"isStart":true})});}
            var Q20;
            {var subQ0=sQuery(id+"F6.wireOp",EDGE,"E86");Q20=makeQuery(id+"F7.boolean.opBoolean","COPY",EDGE,{"disambiguationData":[topologyDisambiguationEdgeConnected([makeQuery(id+"F1.opExtrude","SWEPT_FACE",FACE,{"disambiguationData":[OSD([sQuery(id+"F0.wireOp",EDGE,"E7")])]})])],"derivedFrom":makeQuery(id+"F7.opExtrude","CAP_EDGE",EDGE,{"disambiguationData":[OSD([subQ0])],"isStart":false})});}
            var Q21;
            {var subQ0=sQuery(id+"F6.wireOp",EDGE,"E86");Q21=makeQuery(id+"F7.boolean.opBoolean","COPY",EDGE,{"disambiguationData":[topologyDisambiguationEdgeConnected([makeQuery(id+"F1.opExtrude","SWEPT_FACE",FACE,{"disambiguationData":[OSD([sQuery(id+"F0.wireOp",EDGE,"E7")])]})])],"derivedFrom":makeQuery(id+"F7.opExtrude","CAP_EDGE",EDGE,{"disambiguationData":[OSD([subQ0])],"isStart":true})});}
            var Q22;
            {var subQ0=sQuery(id+"F6.wireOp",EDGE,"E86");Q22=makeQuery(id+"F7.boolean.opBoolean","COPY",EDGE,{"disambiguationData":[topologyDisambiguationEdgeConnected([makeQuery(id+"F1.opExtrude","SWEPT_FACE",FACE,{"disambiguationData":[OSD([sQuery(id+"F0.wireOp",EDGE,"E3")])]})])],"derivedFrom":makeQuery(id+"F7.opExtrude","CAP_EDGE",EDGE,{"disambiguationData":[OSD([subQ0])],"isStart":false})});}
            var Q23;
            {var subQ0=sQuery(id+"F6.wireOp",EDGE,"E86");Q23=makeQuery(id+"F7.boolean.opBoolean","COPY",EDGE,{"disambiguationData":[topologyDisambiguationEdgeConnected([makeQuery(id+"F1.opExtrude","SWEPT_FACE",FACE,{"disambiguationData":[OSD([sQuery(id+"F0.wireOp",EDGE,"E3")])]})])],"derivedFrom":makeQuery(id+"F7.opExtrude","CAP_EDGE",EDGE,{"disambiguationData":[OSD([subQ0])],"isStart":true})});}
            var Q24;
            {var subQ0=sQuery(id+"F6.wireOp",EDGE,"E86");Q24=makeQuery(id+"F7.boolean.opBoolean","COPY",EDGE,{"disambiguationData":[topologyDisambiguationEdgeConnected([makeQuery(id+"F1.opExtrude","SWEPT_FACE",FACE,{"disambiguationData":[OSD([sQuery(id+"F0.wireOp",EDGE,"E79")])]})])],"derivedFrom":makeQuery(id+"F7.opExtrude","CAP_EDGE",EDGE,{"disambiguationData":[OSD([subQ0])],"isStart":false})});}
            var Q25;
            {var subQ0=sQuery(id+"F6.wireOp",EDGE,"E86");Q25=makeQuery(id+"F7.boolean.opBoolean","COPY",EDGE,{"disambiguationData":[topologyDisambiguationEdgeConnected([makeQuery(id+"F1.opExtrude","SWEPT_FACE",FACE,{"disambiguationData":[OSD([sQuery(id+"F0.wireOp",EDGE,"E79")])]})])],"derivedFrom":makeQuery(id+"F7.opExtrude","CAP_EDGE",EDGE,{"disambiguationData":[OSD([subQ0])],"isStart":true})});}
            var Q26;
            {var subQ0=sQuery(id+"F6.wireOp",EDGE,"E86");Q26=makeQuery(id+"F7.boolean.opBoolean","COPY",EDGE,{"disambiguationData":[topologyDisambiguationEdgeConnected([makeQuery(id+"F1.opExtrude","SWEPT_FACE",FACE,{"disambiguationData":[OSD([sQuery(id+"F0.wireOp",EDGE,"E75")])]})])],"derivedFrom":makeQuery(id+"F7.opExtrude","CAP_EDGE",EDGE,{"disambiguationData":[OSD([subQ0])],"isStart":false})});}
            var Q27;
            {var subQ0=sQuery(id+"F6.wireOp",EDGE,"E86");Q27=makeQuery(id+"F7.boolean.opBoolean","COPY",EDGE,{"disambiguationData":[topologyDisambiguationEdgeConnected([makeQuery(id+"F1.opExtrude","SWEPT_FACE",FACE,{"disambiguationData":[OSD([sQuery(id+"F0.wireOp",EDGE,"E75")])]})])],"derivedFrom":makeQuery(id+"F7.opExtrude","CAP_EDGE",EDGE,{"disambiguationData":[OSD([subQ0])],"isStart":true})});}
            var Q28;
            {var subQ0=sQuery(id+"F6.wireOp",EDGE,"E86");Q28=makeQuery(id+"F7.boolean.opBoolean","COPY",EDGE,{"disambiguationData":[topologyDisambiguationEdgeConnected([makeQuery(id+"F1.opExtrude","SWEPT_FACE",FACE,{"disambiguationData":[OSD([sQuery(id+"F0.wireOp",EDGE,"E71")])]})])],"derivedFrom":makeQuery(id+"F7.opExtrude","CAP_EDGE",EDGE,{"disambiguationData":[OSD([subQ0])],"isStart":false})});}
            var Q29;
            {var subQ0=sQuery(id+"F6.wireOp",EDGE,"E86");Q29=makeQuery(id+"F7.boolean.opBoolean","COPY",EDGE,{"disambiguationData":[topologyDisambiguationEdgeConnected([makeQuery(id+"F1.opExtrude","SWEPT_FACE",FACE,{"disambiguationData":[OSD([sQuery(id+"F0.wireOp",EDGE,"E71")])]})])],"derivedFrom":makeQuery(id+"F7.opExtrude","CAP_EDGE",EDGE,{"disambiguationData":[OSD([subQ0])],"isStart":true})});}
            var Q30;
            {var subQ0=sQuery(id+"F6.wireOp",EDGE,"E86");Q30=makeQuery(id+"F7.boolean.opBoolean","COPY",EDGE,{"disambiguationData":[topologyDisambiguationEdgeConnected([makeQuery(id+"F1.opExtrude","SWEPT_FACE",FACE,{"disambiguationData":[OSD([sQuery(id+"F0.wireOp",EDGE,"E67")])]})])],"derivedFrom":makeQuery(id+"F7.opExtrude","CAP_EDGE",EDGE,{"disambiguationData":[OSD([subQ0])],"isStart":false})});}
            var Q31;
            {var subQ0=sQuery(id+"F6.wireOp",EDGE,"E86");Q31=makeQuery(id+"F7.boolean.opBoolean","COPY",EDGE,{"disambiguationData":[topologyDisambiguationEdgeConnected([makeQuery(id+"F1.opExtrude","SWEPT_FACE",FACE,{"disambiguationData":[OSD([sQuery(id+"F0.wireOp",EDGE,"E67")])]})])],"derivedFrom":makeQuery(id+"F7.opExtrude","CAP_EDGE",EDGE,{"disambiguationData":[OSD([subQ0])],"isStart":true})});}
            var Q32;
            {var subQ0=sQuery(id+"F6.wireOp",EDGE,"E86");Q32=makeQuery(id+"F7.boolean.opBoolean","COPY",EDGE,{"disambiguationData":[topologyDisambiguationEdgeConnected([makeQuery(id+"F1.opExtrude","SWEPT_FACE",FACE,{"disambiguationData":[OSD([sQuery(id+"F0.wireOp",EDGE,"E63")])]})])],"derivedFrom":makeQuery(id+"F7.opExtrude","CAP_EDGE",EDGE,{"disambiguationData":[OSD([subQ0])],"isStart":false})});}
            var Q33;
            {var subQ0=sQuery(id+"F6.wireOp",EDGE,"E86");Q33=makeQuery(id+"F7.boolean.opBoolean","COPY",EDGE,{"disambiguationData":[topologyDisambiguationEdgeConnected([makeQuery(id+"F1.opExtrude","SWEPT_FACE",FACE,{"disambiguationData":[OSD([sQuery(id+"F0.wireOp",EDGE,"E63")])]})])],"derivedFrom":makeQuery(id+"F7.opExtrude","CAP_EDGE",EDGE,{"disambiguationData":[OSD([subQ0])],"isStart":true})});}
            var Q34;
            {var subQ0=sQuery(id+"F6.wireOp",EDGE,"E86");Q34=makeQuery(id+"F7.boolean.opBoolean","COPY",EDGE,{"disambiguationData":[topologyDisambiguationEdgeConnected([makeQuery(id+"F1.opExtrude","SWEPT_FACE",FACE,{"disambiguationData":[OSD([sQuery(id+"F0.wireOp",EDGE,"E59")])]})])],"derivedFrom":makeQuery(id+"F7.opExtrude","CAP_EDGE",EDGE,{"disambiguationData":[OSD([subQ0])],"isStart":false})});}
            var Q35;
            {var subQ0=sQuery(id+"F6.wireOp",EDGE,"E86");Q35=makeQuery(id+"F7.boolean.opBoolean","COPY",EDGE,{"disambiguationData":[topologyDisambiguationEdgeConnected([makeQuery(id+"F1.opExtrude","SWEPT_FACE",FACE,{"disambiguationData":[OSD([sQuery(id+"F0.wireOp",EDGE,"E59")])]})])],"derivedFrom":makeQuery(id+"F7.opExtrude","CAP_EDGE",EDGE,{"disambiguationData":[OSD([subQ0])],"isStart":true})});}
            var Q36;
            {var subQ0=sQuery(id+"F6.wireOp",EDGE,"E86");Q36=makeQuery(id+"F7.boolean.opBoolean","COPY",EDGE,{"disambiguationData":[topologyDisambiguationEdgeConnected([makeQuery(id+"F1.opExtrude","SWEPT_FACE",FACE,{"disambiguationData":[OSD([sQuery(id+"F0.wireOp",EDGE,"E55")])]})])],"derivedFrom":makeQuery(id+"F7.opExtrude","CAP_EDGE",EDGE,{"disambiguationData":[OSD([subQ0])],"isStart":false})});}
            var Q37;
            {var subQ0=sQuery(id+"F6.wireOp",EDGE,"E86");Q37=makeQuery(id+"F7.boolean.opBoolean","COPY",EDGE,{"disambiguationData":[topologyDisambiguationEdgeConnected([makeQuery(id+"F1.opExtrude","SWEPT_FACE",FACE,{"disambiguationData":[OSD([sQuery(id+"F0.wireOp",EDGE,"E55")])]})])],"derivedFrom":makeQuery(id+"F7.opExtrude","CAP_EDGE",EDGE,{"disambiguationData":[OSD([subQ0])],"isStart":true})});}
            var Q38;
            {var subQ0=sQuery(id+"F6.wireOp",EDGE,"E86");Q38=makeQuery(id+"F7.boolean.opBoolean","COPY",EDGE,{"disambiguationData":[topologyDisambiguationEdgeConnected([makeQuery(id+"F1.opExtrude","SWEPT_FACE",FACE,{"disambiguationData":[OSD([sQuery(id+"F0.wireOp",EDGE,"E51")])]})])],"derivedFrom":makeQuery(id+"F7.opExtrude","CAP_EDGE",EDGE,{"disambiguationData":[OSD([subQ0])],"isStart":false})});}
            var Q39;
            {var subQ0=sQuery(id+"F6.wireOp",EDGE,"E86");Q39=makeQuery(id+"F7.boolean.opBoolean","COPY",EDGE,{"disambiguationData":[topologyDisambiguationEdgeConnected([makeQuery(id+"F1.opExtrude","SWEPT_FACE",FACE,{"disambiguationData":[OSD([sQuery(id+"F0.wireOp",EDGE,"E51")])]})])],"derivedFrom":makeQuery(id+"F7.opExtrude","CAP_EDGE",EDGE,{"disambiguationData":[OSD([subQ0])],"isStart":true})});}
            chamfer(context, id + "F10", {"entities" : qUnion([Q0, Q1, Q2, Q3, Q4, Q5, Q6, Q7, Q8, Q9, Q10, Q11, Q12, Q13, Q14, Q15, Q16, Q17, Q18, Q19, Q20, Q21, Q22, Q23, Q24, Q25, Q26, Q27, Q28, Q29, Q30, Q31, Q32, Q33, Q34, Q35, Q36, Q37, Q38, Q39]), "width" : .1 * mm, "tangentPropagation" : true});
        }
        {
            var Q0;
            Q0=makeQuery(id+"F1.opExtrude","CAP_FACE",FACE,{"disambiguationData":[OSD([sQuery(id+"F0.wireOp",EDGE,"E0"),sQuery(id+"F0.wireOp",EDGE,"E1"),sQuery(id+"F0.wireOp",EDGE,"E2"),sQuery(id+"F0.wireOp",EDGE,"E3"),sQuery(id+"F0.wireOp",EDGE,"E4"),sQuery(id+"F0.wireOp",EDGE,"E5"),sQuery(id+"F0.wireOp",EDGE,"E6"),sQuery(id+"F0.wireOp",EDGE,"E7"),sQuery(id+"F0.wireOp",EDGE,"E8"),sQuery(id+"F0.wireOp",EDGE,"E9"),sQuery(id+"F0.wireOp",EDGE,"E10"),sQuery(id+"F0.wireOp",EDGE,"E11"),sQuery(id+"F0.wireOp",EDGE,"E12"),sQuery(id+"F0.wireOp",EDGE,"E13"),sQuery(id+"F0.wireOp",EDGE,"E14"),sQuery(id+"F0.wireOp",EDGE,"E15"),sQuery(id+"F0.wireOp",EDGE,"E16"),sQuery(id+"F0.wireOp",EDGE,"E17"),sQuery(id+"F0.wireOp",EDGE,"E18"),sQuery(id+"F0.wireOp",EDGE,"E19"),sQuery(id+"F0.wireOp",EDGE,"E20"),sQuery(id+"F0.wireOp",EDGE,"E21"),sQuery(id+"F0.wireOp",EDGE,"E22"),sQuery(id+"F0.wireOp",EDGE,"E23"),sQuery(id+"F0.wireOp",EDGE,"E24"),sQuery(id+"F0.wireOp",EDGE,"E25"),sQuery(id+"F0.wireOp",EDGE,"E26"),sQuery(id+"F0.wireOp",EDGE,"E27"),sQuery(id+"F0.wireOp",EDGE,"E28"),sQuery(id+"F0.wireOp",EDGE,"E29"),sQuery(id+"F0.wireOp",EDGE,"E30"),sQuery(id+"F0.wireOp",EDGE,"E31"),sQuery(id+"F0.wireOp",EDGE,"E32"),sQuery(id+"F0.wireOp",EDGE,"E33"),sQuery(id+"F0.wireOp",EDGE,"E34"),sQuery(id+"F0.wireOp",EDGE,"E35"),sQuery(id+"F0.wireOp",EDGE,"E36"),sQuery(id+"F0.wireOp",EDGE,"E37"),sQuery(id+"F0.wireOp",EDGE,"E38"),sQuery(id+"F0.wireOp",EDGE,"E39"),sQuery(id+"F0.wireOp",EDGE,"E40"),sQuery(id+"F0.wireOp",EDGE,"E41"),sQuery(id+"F0.wireOp",EDGE,"E42"),sQuery(id+"F0.wireOp",EDGE,"E43"),sQuery(id+"F0.wireOp",EDGE,"E44"),sQuery(id+"F0.wireOp",EDGE,"E45"),sQuery(id+"F0.wireOp",EDGE,"E46"),sQuery(id+"F0.wireOp",EDGE,"E47"),sQuery(id+"F0.wireOp",EDGE,"E48"),sQuery(id+"F0.wireOp",EDGE,"E49"),sQuery(id+"F0.wireOp",EDGE,"E50"),sQuery(id+"F0.wireOp",EDGE,"E51"),sQuery(id+"F0.wireOp",EDGE,"E52"),sQuery(id+"F0.wireOp",EDGE,"E53"),sQuery(id+"F0.wireOp",EDGE,"E54"),sQuery(id+"F0.wireOp",EDGE,"E55"),sQuery(id+"F0.wireOp",EDGE,"E56"),sQuery(id+"F0.wireOp",EDGE,"E57"),sQuery(id+"F0.wireOp",EDGE,"E58"),sQuery(id+"F0.wireOp",EDGE,"E59"),sQuery(id+"F0.wireOp",EDGE,"E60"),sQuery(id+"F0.wireOp",EDGE,"E61"),sQuery(id+"F0.wireOp",EDGE,"E62"),sQuery(id+"F0.wireOp",EDGE,"E63"),sQuery(id+"F0.wireOp",EDGE,"E64"),sQuery(id+"F0.wireOp",EDGE,"E65"),sQuery(id+"F0.wireOp",EDGE,"E66"),sQuery(id+"F0.wireOp",EDGE,"E67"),sQuery(id+"F0.wireOp",EDGE,"E68"),sQuery(id+"F0.wireOp",EDGE,"E69"),sQuery(id+"F0.wireOp",EDGE,"E70"),sQuery(id+"F0.wireOp",EDGE,"E71"),sQuery(id+"F0.wireOp",EDGE,"E72"),sQuery(id+"F0.wireOp",EDGE,"E73"),sQuery(id+"F0.wireOp",EDGE,"E74"),sQuery(id+"F0.wireOp",EDGE,"E75"),sQuery(id+"F0.wireOp",EDGE,"E76"),sQuery(id+"F0.wireOp",EDGE,"E77"),sQuery(id+"F0.wireOp",EDGE,"E78"),sQuery(id+"F0.wireOp",EDGE,"E79")])],"isStart":true});
            var sketch = newSketch(context, id + "F11", { "sketchPlane" : qUnion([Q0])});
            skPoint(sketch, "E87.0", {"position": v(0, 0) * mm});
            skSolve(sketch);
        }
        {
            var Q0;
            Q0=sQuery(id+"F11.wireOp",VERTEX,"E87.0");
            var Q1;
            Q1=makeQuery(id+"F1.opExtrude","SWEPT_BODY",BODY,{"disambiguationData":[OSD([sQuery(id+"F0.wireOp",EDGE,"E0"),sQuery(id+"F0.wireOp",EDGE,"E1"),sQuery(id+"F0.wireOp",EDGE,"E2"),sQuery(id+"F0.wireOp",EDGE,"E3"),sQuery(id+"F0.wireOp",EDGE,"E4"),sQuery(id+"F0.wireOp",EDGE,"E5"),sQuery(id+"F0.wireOp",EDGE,"E6"),sQuery(id+"F0.wireOp",EDGE,"E7"),sQuery(id+"F0.wireOp",EDGE,"E8"),sQuery(id+"F0.wireOp",EDGE,"E9"),sQuery(id+"F0.wireOp",EDGE,"E10"),sQuery(id+"F0.wireOp",EDGE,"E11"),sQuery(id+"F0.wireOp",EDGE,"E12"),sQuery(id+"F0.wireOp",EDGE,"E13"),sQuery(id+"F0.wireOp",EDGE,"E14"),sQuery(id+"F0.wireOp",EDGE,"E15"),sQuery(id+"F0.wireOp",EDGE,"E16"),sQuery(id+"F0.wireOp",EDGE,"E17"),sQuery(id+"F0.wireOp",EDGE,"E18"),sQuery(id+"F0.wireOp",EDGE,"E19"),sQuery(id+"F0.wireOp",EDGE,"E20"),sQuery(id+"F0.wireOp",EDGE,"E21"),sQuery(id+"F0.wireOp",EDGE,"E22"),sQuery(id+"F0.wireOp",EDGE,"E23"),sQuery(id+"F0.wireOp",EDGE,"E24"),sQuery(id+"F0.wireOp",EDGE,"E25"),sQuery(id+"F0.wireOp",EDGE,"E26"),sQuery(id+"F0.wireOp",EDGE,"E27"),sQuery(id+"F0.wireOp",EDGE,"E28"),sQuery(id+"F0.wireOp",EDGE,"E29"),sQuery(id+"F0.wireOp",EDGE,"E30"),sQuery(id+"F0.wireOp",EDGE,"E31"),sQuery(id+"F0.wireOp",EDGE,"E32"),sQuery(id+"F0.wireOp",EDGE,"E33"),sQuery(id+"F0.wireOp",EDGE,"E34"),sQuery(id+"F0.wireOp",EDGE,"E35"),sQuery(id+"F0.wireOp",EDGE,"E36"),sQuery(id+"F0.wireOp",EDGE,"E37"),sQuery(id+"F0.wireOp",EDGE,"E38"),sQuery(id+"F0.wireOp",EDGE,"E39"),sQuery(id+"F0.wireOp",EDGE,"E40"),sQuery(id+"F0.wireOp",EDGE,"E41"),sQuery(id+"F0.wireOp",EDGE,"E42"),sQuery(id+"F0.wireOp",EDGE,"E43"),sQuery(id+"F0.wireOp",EDGE,"E44"),sQuery(id+"F0.wireOp",EDGE,"E45"),sQuery(id+"F0.wireOp",EDGE,"E46"),sQuery(id+"F0.wireOp",EDGE,"E47"),sQuery(id+"F0.wireOp",EDGE,"E48"),sQuery(id+"F0.wireOp",EDGE,"E49"),sQuery(id+"F0.wireOp",EDGE,"E50"),sQuery(id+"F0.wireOp",EDGE,"E51"),sQuery(id+"F0.wireOp",EDGE,"E52"),sQuery(id+"F0.wireOp",EDGE,"E53"),sQuery(id+"F0.wireOp",EDGE,"E54"),sQuery(id+"F0.wireOp",EDGE,"E55"),sQuery(id+"F0.wireOp",EDGE,"E56"),sQuery(id+"F0.wireOp",EDGE,"E57"),sQuery(id+"F0.wireOp",EDGE,"E58"),sQuery(id+"F0.wireOp",EDGE,"E59"),sQuery(id+"F0.wireOp",EDGE,"E60"),sQuery(id+"F0.wireOp",EDGE,"E61"),sQuery(id+"F0.wireOp",EDGE,"E62"),sQuery(id+"F0.wireOp",EDGE,"E63"),sQuery(id+"F0.wireOp",EDGE,"E64"),sQuery(id+"F0.wireOp",EDGE,"E65"),sQuery(id+"F0.wireOp",EDGE,"E66"),sQuery(id+"F0.wireOp",EDGE,"E67"),sQuery(id+"F0.wireOp",EDGE,"E68"),sQuery(id+"F0.wireOp",EDGE,"E69"),sQuery(id+"F0.wireOp",EDGE,"E70"),sQuery(id+"F0.wireOp",EDGE,"E71"),sQuery(id+"F0.wireOp",EDGE,"E72"),sQuery(id+"F0.wireOp",EDGE,"E73"),sQuery(id+"F0.wireOp",EDGE,"E74"),sQuery(id+"F0.wireOp",EDGE,"E75"),sQuery(id+"F0.wireOp",EDGE,"E76"),sQuery(id+"F0.wireOp",EDGE,"E77"),sQuery(id+"F0.wireOp",EDGE,"E78"),sQuery(id+"F0.wireOp",EDGE,"E79")])]});
            hole(context, id + "F12", {"style" : HoleStyle.C_SINK, "endStyle" : HoleEndStyle.BLIND, "holeDiameter" : 8.5 * mm, "cSinkDiameter" : 11 * mm, "cSinkAngle" : 90 * degree, "holeDepth" : 40 * mm, "tappedDepth" : 35.5 * mm, "tapClearance" : 3, "locations" : qUnion([Q0]), "scope" : qUnion([Q1])});
        }
    });
